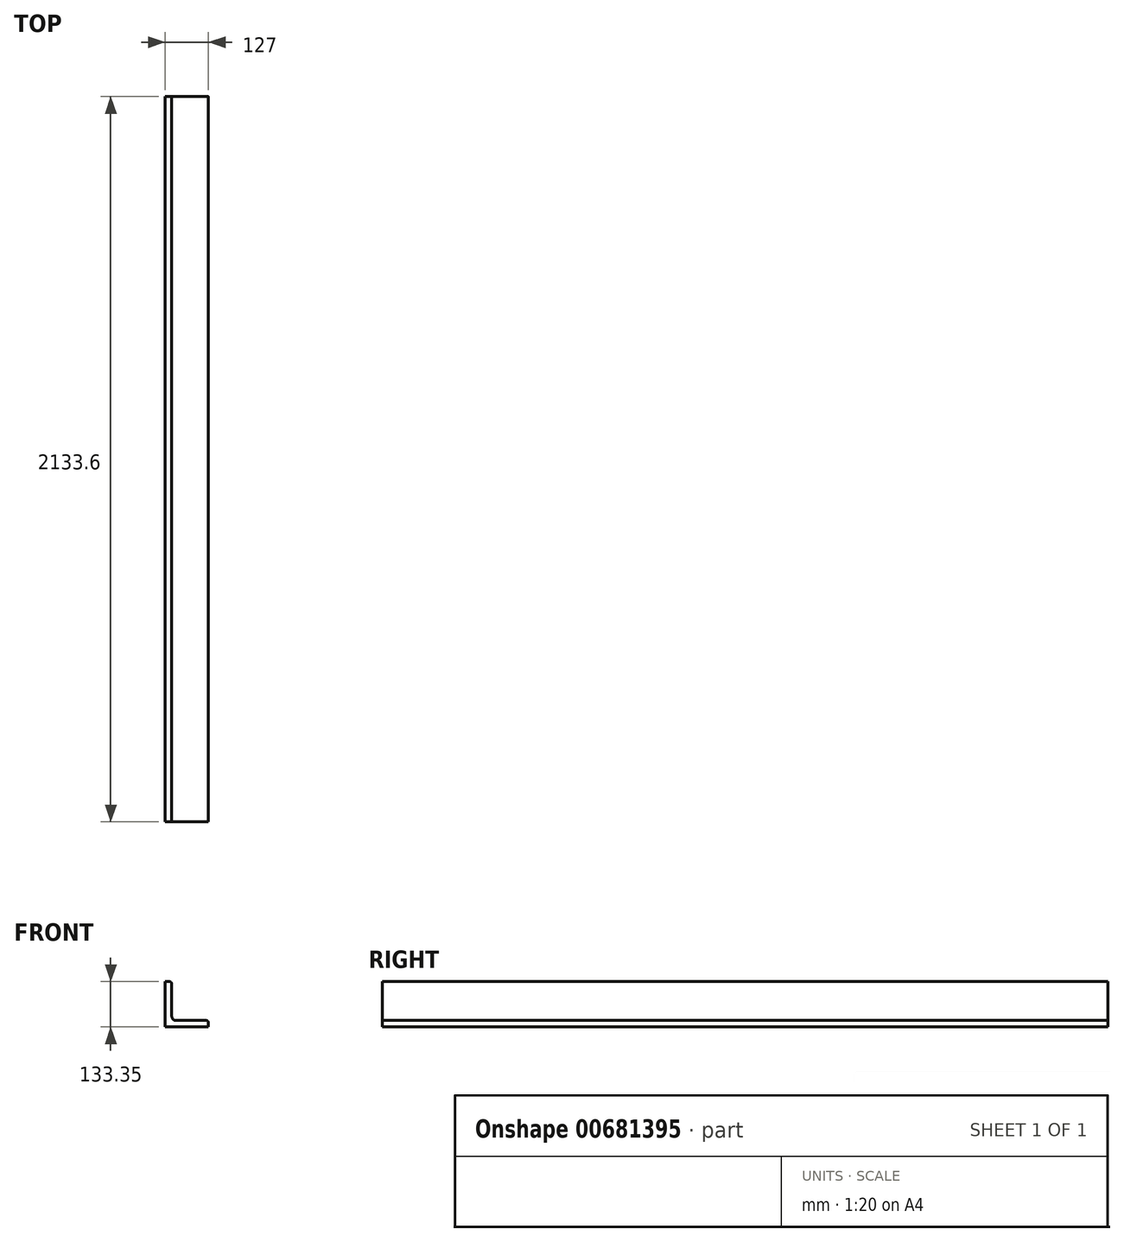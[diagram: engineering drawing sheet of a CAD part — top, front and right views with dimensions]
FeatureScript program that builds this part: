
annotation { "Feature Type Name" : "Feature", "Feature Type Description" : "" }
export const myFeature = defineFeature(function(context is Context, id is Id, definition is map)
    precondition{}
    {
        {
            var Q0;
            Q0=qCreatedBy(makeId("Front.planeOp"),FACE);
            var sketch = newSketch(context, id + "F0", { "sketchPlane" : qUnion([Q0])});
            skLineSegment(sketch, "E0", {"start": v(0, 0) * mm, "end": v(-63.5, 0) * mm});
            skLineSegment(sketch, "E1", {"start": v(-63.5, 0) * mm, "end": v(-63.5, 63.5) * mm});
            skLineSegment(sketch, "E2", {"start": v(-63.5, 63.5) * mm, "end": v(-50.8, 63.5) * mm});
            skLineSegment(sketch, "E3", {"start": v(-44.45, -69.85) * mm, "end": v(63.5, -69.85) * mm});
            skLineSegment(sketch, "E4", {"start": v(63.5, -69.85) * mm, "end": v(63.5, -57.15) * mm});
            skLineSegment(sketch, "E5", {"start": v(-63.5, -44.45) * mm, "end": v(-63.5, -69.85) * mm});
            skLineSegment(sketch, "E6", {"start": v(-63.5, -69.85) * mm, "end": v(-44.45, -69.85) * mm});
            skLineSegment(sketch, "E7", {"start": v(-63.5, 0) * mm, "end": v(-63.5, -44.45) * mm});
            skLineSegment(sketch, "E8", {"start": v(-44.45, 57.15) * mm, "end": v(-44.45, -38.1) * mm});
            skLineSegment(sketch, "E9", {"start": v(-31.75, -50.8) * mm, "end": v(57.15, -50.8) * mm});
            skPoint(sketch, "E10.visualSharp", {"position": v(-44.45, 63.5) * mm});
            skArc(sketch, "E10.filletArc", {"start": v(-44.45, 57.15) * mm, "mid": v(-46.3, 61.64) * mm, "end": v(-50.8, 63.5) * mm});
            skPoint(sketch, "E11.visualSharp", {"position": v(-44.45, -50.8) * mm});
            skArc(sketch, "E11.filletArc", {"start": v(-44.45, -38.1) * mm, "mid": v(-40.73, -47.08) * mm, "end": v(-31.75, -50.8) * mm});
            skPoint(sketch, "E12.visualSharp", {"position": v(63.5, -50.8) * mm});
            skArc(sketch, "E12.filletArc", {"start": v(63.5, -57.15) * mm, "mid": v(61.64, -52.66) * mm, "end": v(57.15, -50.8) * mm});
            skSolve(sketch);
        }
        {
            var Q0;
            Q0 = qSketchRegion(id + "F0", true);
            extrude(context, id + "F1", {"entities" : qUnion([Q0]), "depth" : 2133.6 * mm, "offsetDistance" : 25.4 * mm});
        }
    });
